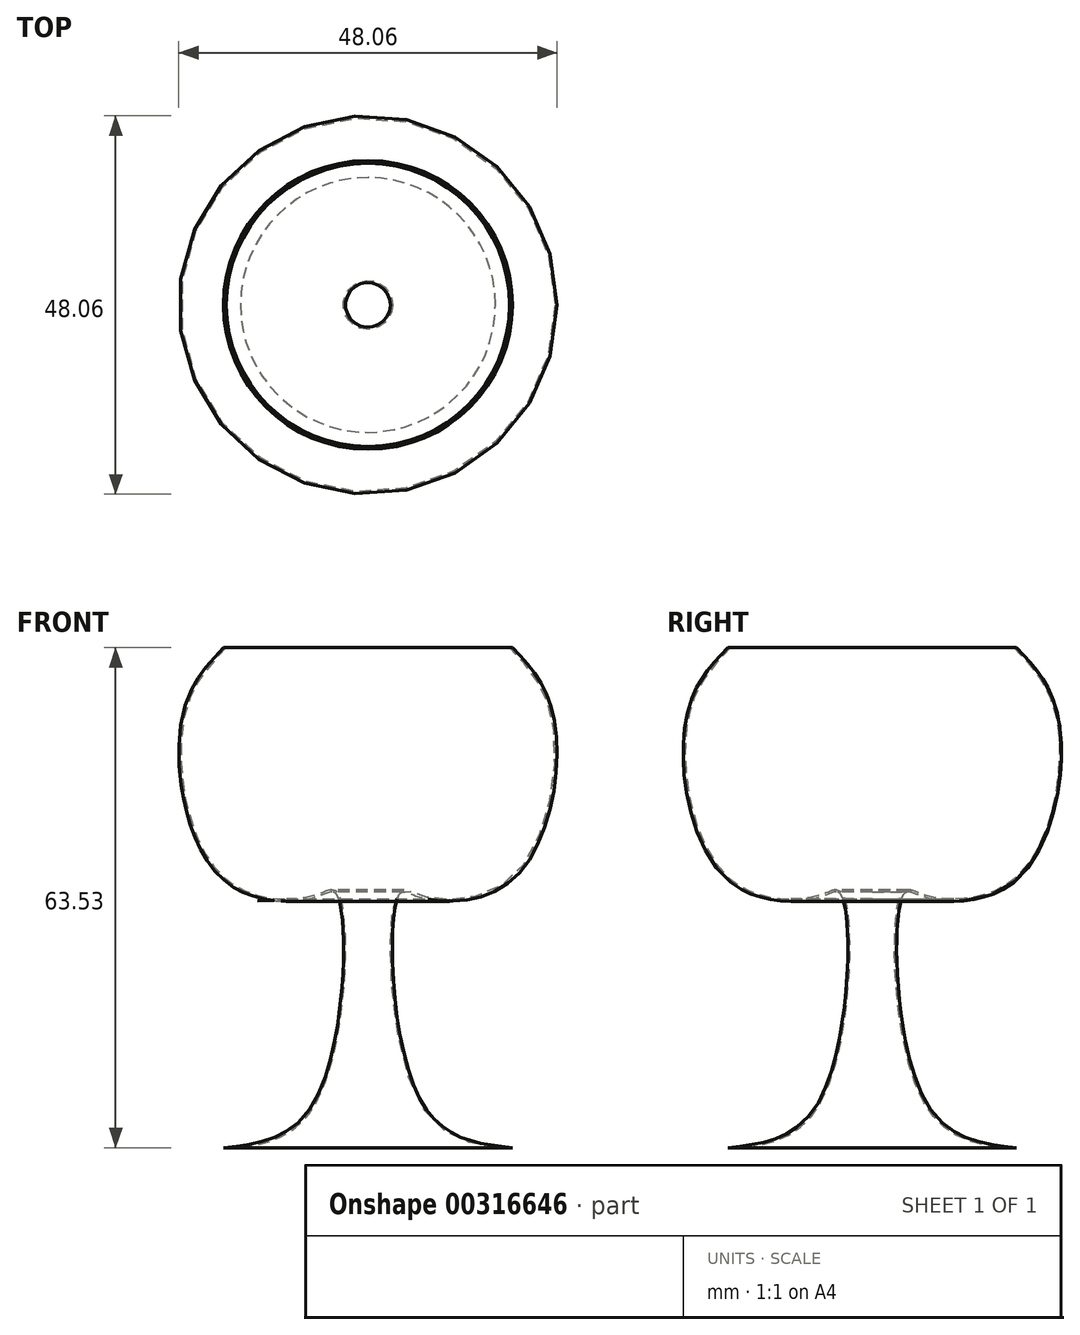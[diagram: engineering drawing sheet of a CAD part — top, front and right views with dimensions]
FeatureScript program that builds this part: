
annotation { "Feature Type Name" : "Feature", "Feature Type Description" : "" }
export const myFeature = defineFeature(function(context is Context, id is Id, definition is map)
    precondition{}
    {
        {
            var Q0;
            Q0=qCreatedBy(makeId("Front.planeOp"),FACE);
            var sketch = newSketch(context, id + "F0", { "sketchPlane" : qUnion([Q0])});
            skLineSegment(sketch, "E0", {"start": v(0, 0) * mm, "end": v(0, 67.52) * mm, "construction": true});
            skLineSegment(sketch, "E1", {"start": v(0, 0) * mm, "end": v(-18.34, 0) * mm});
            skFitSpline(sketch, "E2", {"points": [v(-18.34, 0) * mm, v(-6.65, 6.11) * mm, v(-3.99, 32.16) * mm, v(-6.38, 31.9) * mm, v(-18.34, 34.02) * mm, v(-23.66, 54.5) * mm, v(-18.34, 63.53) * mm], "startDerivative": vector(79.96, 8.76) * mm, "endDerivative": vector(44.88, 47.25) * mm});
            skLineSegment(sketch, "E3", {"start": v(-18.34, 63.53) * mm, "end": v(0, 63.53) * mm});
            skLineSegment(sketch, "E4", {"start": v(0, 63.53) * mm, "end": v(0, 0) * mm});
            skSolve(sketch);
        }
        {
            var Q0;
            Q0=makeQuery(id+"F0.imprint","IMPRINT",FACE,{"disambiguationData":[TD([[makeQuery(id+"F0.imprint","IMPRINT",EDGE,{"derivedFrom":sQuery(id+"F0.wireOp",EDGE,"E1")}),-1.0]])]});
            var Q1;
            Q1=sQuery(id+"F0.wireOp",EDGE,"E4");
            revolve(context, id + "F1", {"entities" : qUnion([Q0]), "axis" : qUnion([Q1]), "revolveType" : RevolveType.FULL});
        }
        {
            var Q0;
            Q0=makeQuery(id+"F1.opRevolve","SWEPT_FACE",FACE,{"disambiguationData":[OSD([sQuery(id+"F0.wireOp",EDGE,"E3")])]});
            var Q1;
            Q1=makeQuery(id+"F1.opRevolve","SWEPT_FACE",FACE,{"disambiguationData":[OSD([sQuery(id+"F0.wireOp",EDGE,"E1")])]});
            shell(context, id + "F2", {"entities" : qUnion([Q0, Q1]), "thickness" : 0.25 * mm});
        }
    });
